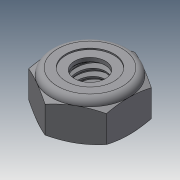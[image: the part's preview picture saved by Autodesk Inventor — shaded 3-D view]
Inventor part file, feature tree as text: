
AUTODESK INVENTOR PART (.ipt)
format: ipt  version: 2018.3 (Build 223284000, 284)  size: 270,336 bytes
history: native  units: in
note: dims shown in document units (in); Inventor stores cm internally (conversion verified against a paired STEP export)
features: other x1, revolve x1
ambient origin geometry x8: Origin, YZ Plane, XZ Plane, XY Plane, X Axis, Y Axis, Z Axis, Center Point
bodies: Solid1 (feature_tree), Solid2 (feature_tree)
feature tree (2):
  other  "Cut-Revolve4"
  revolve  "Revolve2"  [1 undecoded]
note: 1 required parameter value undecoded (feature->parameter linkage not recoverable at this tier; creation-order binding heuristic only, values carry confidence <= 0.55)
